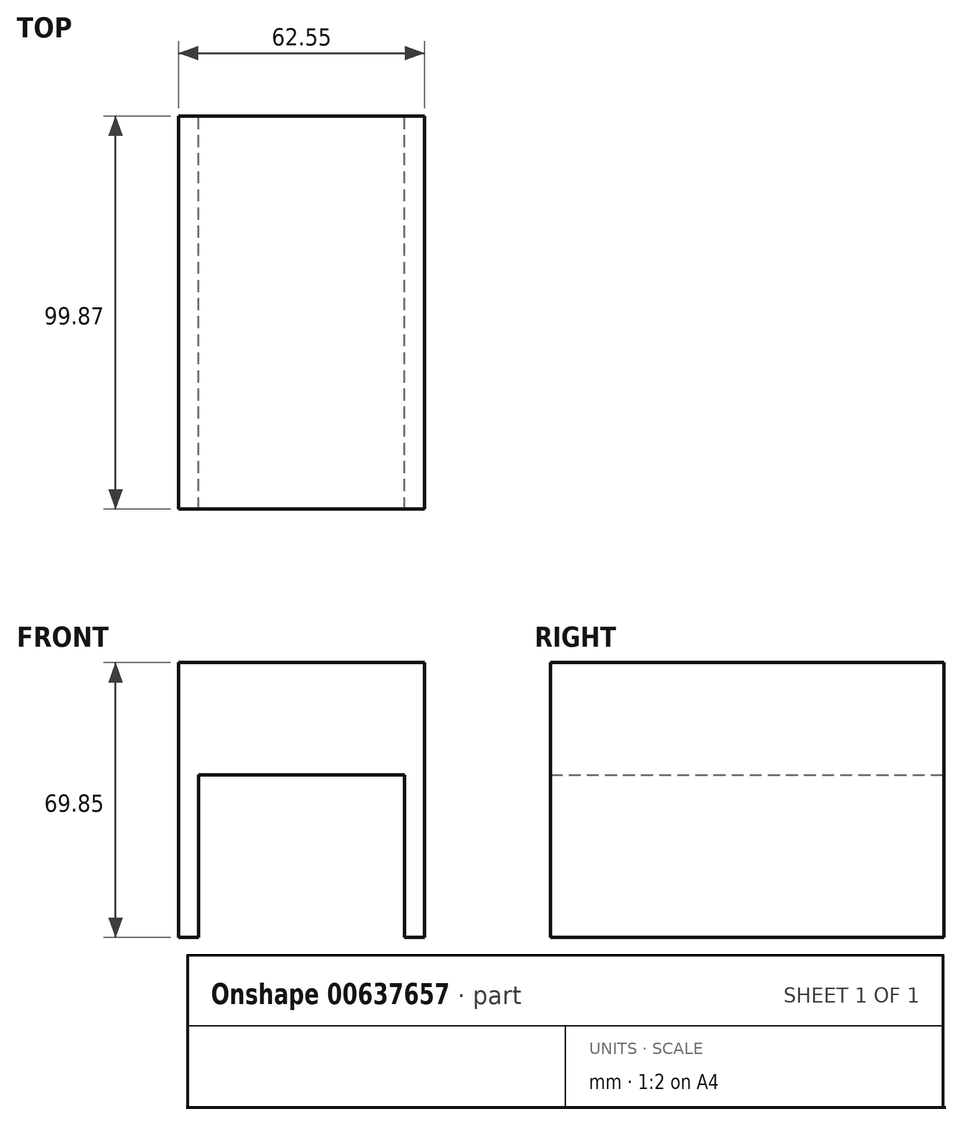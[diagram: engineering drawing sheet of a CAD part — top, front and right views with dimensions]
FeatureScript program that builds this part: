
annotation { "Feature Type Name" : "Feature", "Feature Type Description" : "" }
export const myFeature = defineFeature(function(context is Context, id is Id, definition is map)
    precondition{}
    {
        {
            var Q0;
            Q0=qCreatedBy(makeId("Front.planeOp"),FACE);
            var sketch = newSketch(context, id + "F0", { "sketchPlane" : qUnion([Q0])});
            skLineSegment(sketch, "E0", {"start": v(-13.71, -48.82) * mm, "end": v(-13.71, 21.03) * mm});
            skLineSegment(sketch, "E1", {"start": v(-13.71, 21.03) * mm, "end": v(48.84, 21.03) * mm});
            skLineSegment(sketch, "E2", {"start": v(48.84, 21.03) * mm, "end": v(48.84, -48.82) * mm});
            skLineSegment(sketch, "E3", {"start": v(-13.71, -48.82) * mm, "end": v(-8.63, -48.82) * mm});
            skLineSegment(sketch, "E4", {"start": v(-8.63, -48.82) * mm, "end": v(-8.63, -7.55) * mm});
            skLineSegment(sketch, "E5", {"start": v(-8.63, -7.55) * mm, "end": v(43.76, -7.55) * mm});
            skLineSegment(sketch, "E6", {"start": v(43.76, -7.55) * mm, "end": v(43.76, -48.82) * mm});
            skLineSegment(sketch, "E7", {"start": v(43.76, -48.82) * mm, "end": v(48.84, -48.82) * mm});
            skSolve(sketch);
        }
        {
            var Q0;
            Q0=makeQuery(id+"F0.imprint","IMPRINT",FACE,{"disambiguationData":[TD([[makeQuery(id+"F0.imprint","IMPRINT",EDGE,{"derivedFrom":sQuery(id+"F0.wireOp",EDGE,"E0")}),-1.0]])]});
            extrude(context, id + "F1", {"entities" : qUnion([Q0]), "depth" : 99.87 * mm, "offsetDistance" : 25.4 * mm});
        }
    });
